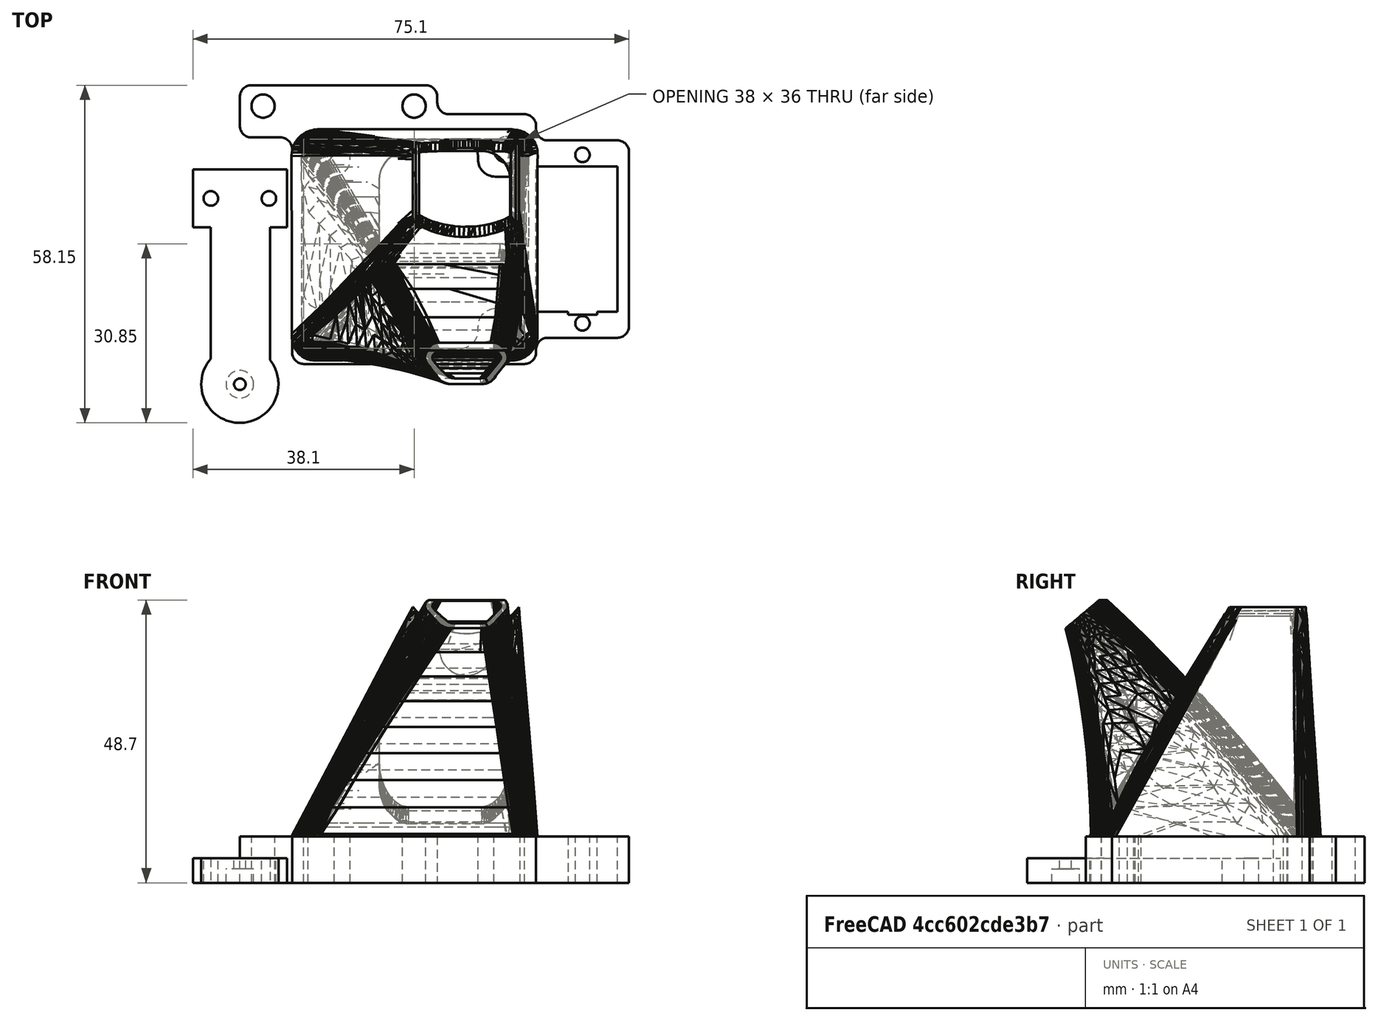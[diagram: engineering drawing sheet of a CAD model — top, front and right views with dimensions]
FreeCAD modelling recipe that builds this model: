
FCSTD DOCUMENT  (FreeCAD 0.16R5165 (Git))
Label: fan_and_servo_mount
License: All rights reserved
LicenseURL: http://en.wikipedia.org/wiki/All_rights_reserved
objects: Part::Cylinder×13, Part::Box×10, Part::Feature×5, Part::MultiFuse×5, Part::Cut×3, Part::Fillet×2, Mesh::Feature×1
note: 38 computed .brp shape members not serialized (recipe doc carries the construction recipe); baked Part::Feature solids carry a one-line shape summary decoded from their .brp

FEATURE [Mesh::Feature] TAZ_Fan_Dual_Duct
FEATURE [Part::Feature] TAZ_Fan_Dual_Duct001
  shape: bbox 51.32 x 51.87 x 48.7 mm, 11704 faces, 0 solids (baked)
FEATURE [Part::Feature] TAZ_Fan_Dual_Duct001001  label="TAZ_Fan_Dual_Duct002"
  shape: bbox 51.32 x 51.87 x 48.7 mm, 9288 faces, 0 solids (baked)
FEATURE [Part::Box] Box
  Height = 8
  Length = 16
  Placement = pos=(51,8,0) rot=(0,0,1;0rad)
  Width = 34
FEATURE [Part::Box] Box001
  Height = 8
  Length = 14
  Placement = pos=(51,12.5,0) rot=(0,0,1;0rad)
  Width = 25
FEATURE [Part::Cylinder] Cylinder
  Angle = 360
  Height = 10
  Placement = pos=(59,39.5,-1) rot=(0,0,1;0rad)
  Radius = 1.25
FEATURE [Part::Cylinder] Cylinder001
  Angle = 360
  Height = 10
  Placement = pos=(59,10.5,-1) rot=(0,0,1;0rad)
  Radius = 1.25
FEATURE [Part::Feature] TAZ_Fan_Dual_Duct001001_solid  label="TAZ_Fan_Dual_Duct002 (Solid)"
  shape: bbox 51.32 x 51.88 x 48.7 mm, 9288 faces (baked)
FEATURE [Part::Cylinder] Cylinder002
  Angle = 360
  Height = 2.36
  Radius = 2.37
FEATURE [Part::Box] Box003
  Height = 4.2
  Length = 10.2
  Placement = pos=(-5,4,0) rot=(0,0,1;0rad)
  Width = 28
FEATURE [Part::Box] Box004
  Height = 8
  Length = 5
  Placement = pos=(56.5,12,0) rot=(0,0,1;0rad)
  Width = 1
FEATURE [Part::Box] Box005
  Height = 4.2
  Length = 16.2
  Placement = pos=(-8.1,27,0) rot=(0,0,1;0rad)
  Width = 10
FEATURE [Part::Cylinder] Cylinder004
  Angle = 360
  Height = 10
  Placement = pos=(5,32,-3) rot=(0,0,1;0rad)
  Radius = 1.25
FEATURE [Part::Cylinder] Cylinder005
  Angle = 360
  Height = 10
  Placement = pos=(-5,32,-3) rot=(0,0,1;0rad)
  Radius = 1.25
FEATURE [Part::Cylinder] Cylinder006
  Angle = 360
  Height = 4.2
  Radius = 6.65
FEATURE [Part::MultiFuse] Fusion003
  Shapes = -> [Box005,Box003,Cylinder006]
FEATURE [Part::Feature] TAZ_Fan_Dual_Duct001002  label="TAZ_Fan_Dual_Duct003"
  shape: bbox 51.32 x 51.87 x 48.7 mm, 9288 faces, 0 solids (baked)
FEATURE [Part::Box] Box006
  Height = 8
  Length = 42
  Placement = pos=(9,3.5,0) rot=(0,0,1;0rad)
  Width = 43
FEATURE [Part::Box] Box007
  Height = 8
  Length = 34
  Placement = pos=(0,42.5,0) rot=(0,0,1;0rad)
  Width = 9
FEATURE [Part::Cylinder] Cylinder007
  Angle = 360
  Height = 8
  Placement = pos=(46,8.4,0) rot=(0,0,1;0rad)
  Radius = 2.25
FEATURE [Part::Cylinder] Cylinder008
  Angle = 360
  Height = 8
  Placement = pos=(46,40.4,0) rot=(0,0,1;0rad)
  Radius = 2.25
FEATURE [Part::Cylinder] Cylinder009
  Angle = 360
  Height = 8
  Placement = pos=(14,40.4,0) rot=(0,0,1;0rad)
  Radius = 2.25
FEATURE [Part::Cylinder] Cylinder010
  Angle = 360
  Height = 8
  Placement = pos=(14,8.4,0) rot=(0,0,1;0rad)
  Radius = 2.25
FEATURE [Part::Cylinder] Cylinder011
  Angle = 360
  Height = 8
  Placement = pos=(30,47.9,0) rot=(0,0,1;0rad)
  Radius = 2
FEATURE [Part::Cylinder] Cylinder012
  Angle = 360
  Height = 8
  Placement = pos=(4,47.9,0) rot=(0,0,1;0rad)
  Radius = 2
FEATURE [Part::Box] Box008
  Height = 8
  Length = 38
  Placement = pos=(11,13,0) rot=(0,0,1;0rad)
  Width = 22.75
FEATURE [Part::Box] Box009
  Height = 8
  Length = 22
  Placement = pos=(19,6.2,0) rot=(0,0,1;0rad)
  Width = 36
FEATURE [Part::MultiFuse] Fusion
  Shapes = -> [Box001,Cylinder008,Cylinder009,Cylinder010,Cylinder011,Box004,Box008,Box009,Cylinder007,Cylinder,Cylinder012,Cylinder001]
FEATURE [Part::MultiFuse] Fusion004
  Shapes = -> [Box,Box006,Box007]
FEATURE [Part::Box] Box010
  Height = 10
  Length = 60
  Placement = pos=(-3,3,-2) rot=(0,0,1;0rad)
  Width = 62
FEATURE [Part::Cut] Cut002002002
  Base = -> TAZ_Fan_Dual_Duct001001_solid
  Tool = -> Box010
FEATURE [Part::Fillet] Fillet
  Base = -> Fusion
  Edges = 12 edges r=3: [Edge45,Edge47,Edge51,Edge55,Edge58,Edge64,Edge71,Edge80,Edge85,Edge86,Edge87,Edge88]
FEATURE [Part::Cut] Cut
  Base = -> Fusion004
  Tool = -> Fillet
FEATURE [Part::Fillet] Fillet001
  Base = -> Cut
  Edges = 12 edges r=2: [Edge1,Edge3,Edge6,Edge23,Edge39,Edge87,Edge125,Edge129,Edge137,Edge167,Edge178,Edge183]
FEATURE [Part::MultiFuse] Fusion005  label="Fan and Servo Mount"
  Shapes = -> [Cut002002002,Fillet001]
FEATURE [Part::Feature] Fusion005001  label="Fan and Servo Mount001"
  shape: bbox 67 x 51.48 x 48.7 mm, 8814 faces (baked)
FEATURE [Part::Cylinder] Cylinder013
  Angle = 360
  Height = 4.2
  Radius = 1
FEATURE [Part::MultiFuse] Fusion005002
  Shapes = -> [Cylinder002,Cylinder004,Cylinder005,Cylinder013]
FEATURE [Part::Cut] Cut002002003  label="Horn"
  Base = -> Fusion003
  Tool = -> Fusion005002
